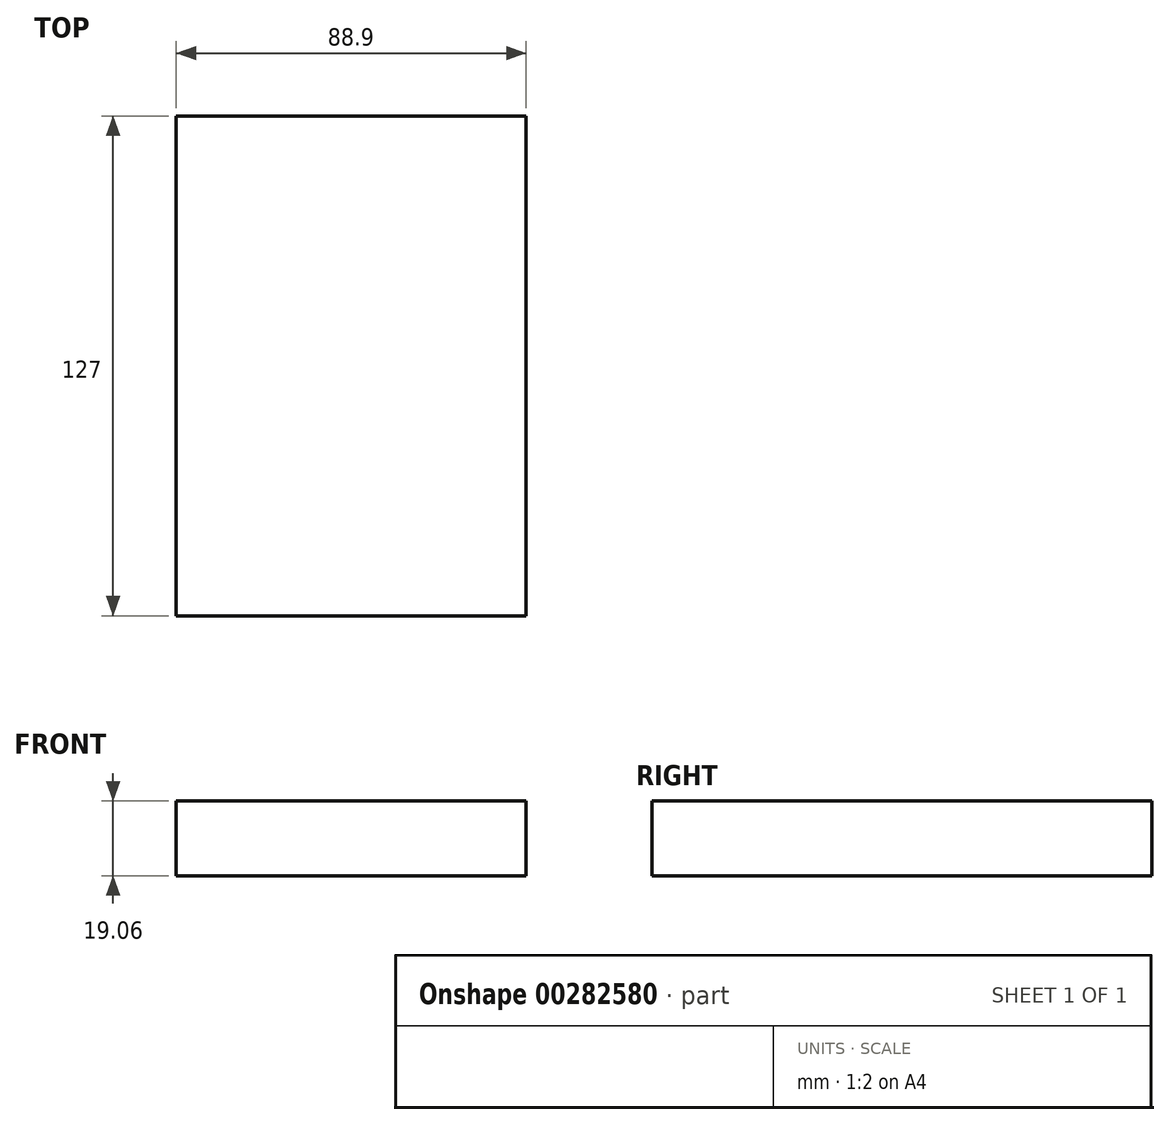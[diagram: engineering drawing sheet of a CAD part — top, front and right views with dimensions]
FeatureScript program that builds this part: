
annotation { "Feature Type Name" : "Feature", "Feature Type Description" : "" }
export const myFeature = defineFeature(function(context is Context, id is Id, definition is map)
    precondition{}
    {
        {
            var Q0;
            Q0=qCreatedBy(makeId("Front.planeOp"),FACE);
            var sketch = newSketch(context, id + "F0", { "sketchPlane" : qUnion([Q0])});
            skLineSegment(sketch, "E0.bottom", {"start": v(44.45, -9.52) * mm, "end": v(-44.45, -9.53) * mm});
            skLineSegment(sketch, "E0.top", {"start": v(44.45, 9.53) * mm, "end": v(-44.45, 9.53) * mm});
            skLineSegment(sketch, "E0.left", {"start": v(44.45, -9.52) * mm, "end": v(44.45, 9.53) * mm});
            skLineSegment(sketch, "E0.right", {"start": v(-44.45, -9.53) * mm, "end": v(-44.45, 9.53) * mm});
            skPoint(sketch, "E0.middle", {"position": v(0, 0) * mm});
            skLineSegment(sketch, "E1.bottom", {"start": v(83.56, 39.78) * mm, "end": v(32.76, 39.78) * mm});
            skLineSegment(sketch, "E1.top", {"start": v(83.56, 68.35) * mm, "end": v(32.76, 68.35) * mm});
            skLineSegment(sketch, "E1.left", {"start": v(83.56, 39.78) * mm, "end": v(83.56, 68.35) * mm});
            skLineSegment(sketch, "E1.right", {"start": v(32.76, 39.78) * mm, "end": v(32.76, 68.35) * mm});
            skPoint(sketch, "E1.middle", {"position": v(58.16, 54.06) * mm});
            skLineSegment(sketch, "E2", {"start": v(16.89, 9.53) * mm, "end": v(16.89, 27) * mm});
            skArc(sketch, "E3", {"start": v(16.89, 27) * mm, "mid": v(21.54, 38.23) * mm, "end": v(32.76, 42.88) * mm});
            skLineSegment(sketch, "E4", {"start": v(32.76, 42.88) * mm, "end": v(58.16, 42.88) * mm});
            skLineSegment(sketch, "E5.0", {"start": v(32.76, 61.93) * mm, "end": v(58.16, 61.93) * mm});
            skArc(sketch, "E5.1", {"start": v(-2.16, 27) * mm, "mid": v(8.07, 51.7) * mm, "end": v(32.76, 61.93) * mm});
            skLineSegment(sketch, "E5.2", {"start": v(-2.16, 9.53) * mm, "end": v(-2.16, 27) * mm});
            skLineSegment(sketch, "E6", {"start": v(58.16, 39.78) * mm, "end": v(58.16, 68.35) * mm});
            skFitSpline(sketch, "E7", {"points": [v(-44.45, 9.52) * mm, v(32.76, 61.93) * mm], "startDerivative": vector(-0.1, 147.86) * mm, "endDerivative": vector(134.78, 2.27) * mm});
            skSolve(sketch);
        }
        {
            var Q0;
            Q0=makeQuery(id+"F0.imprint","IMPRINT",FACE,{"disambiguationData":[TD([[makeQuery(id+"F0.imprint","IMPRINT",EDGE,{"derivedFrom":sQuery(id+"F0.wireOp",EDGE,"E0.bottom")}),-1.0]])]});
            extrude(context, id + "F1", {"entities" : qUnion([Q0]), "endBound" : BoundingType.SYMMETRIC, "depth" : 127 * mm});
        }
    });
